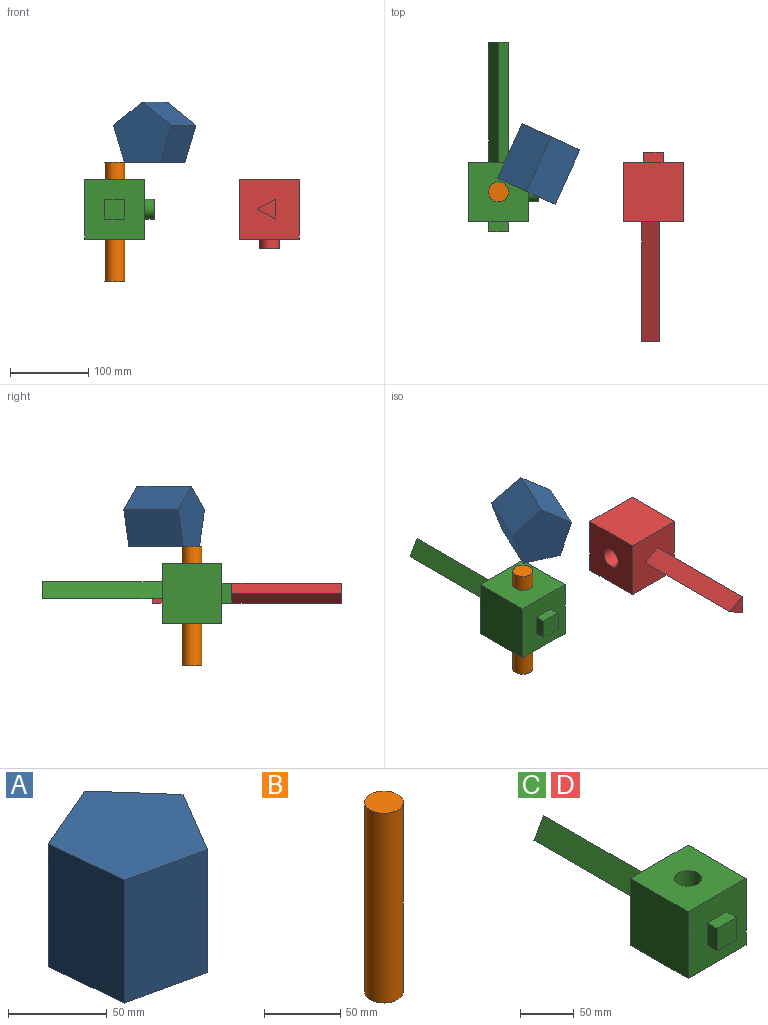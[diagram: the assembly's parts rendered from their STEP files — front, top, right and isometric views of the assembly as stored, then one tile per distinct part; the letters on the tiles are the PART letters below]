
ASSEMBLY  parts=4 mates=3
PART A: 7 faces, bbox 78.8x80.4x76.2 mm
  f0: plane 76.2x37.41mm, normal (0.75,0.66,0), area 3801.5mm2, adj f1,f4,f5,f6
  f1: plane 76.2x45.78mm, normal (-0.4,0.92,0), area 3801.5mm2, adj f0,f2,f5,f6
  f2: plane 76.2x49.66mm, normal (-1,-0.09,0), area 3801.5mm2, adj f1,f3,f5,f6
  f3: plane 76.2x48.69mm, normal (-0.22,-0.98,0), area 3801.5mm2, adj f2,f4,f5,f6
  f4: plane 76.2x42.95mm, normal (0.86,-0.51,0), area 3801.5mm2, adj f0,f3,f5,f6
  f5: plane 80.36x78.79mm, normal (0,0,1), area 4282mm2, adj f0,f1,f2,f3,f4
  f6: plane 80.36x78.79mm, normal (0,0,-1), area 4282mm2, adj f0,f1,f2,f3,f4
PART B: 3 faces, bbox 25.4x25.4x152.4 mm
  f0: cylinder r=12.7mm len=152.4mm, axis (0,0,-1), area 12161mm2, adj f1,f2
  f1: plane 25.4x25.4mm, normal (0,0,1), area 506.7mm2, adj f0
  f2: plane 25.4x25.4mm, normal (0,0,-1), area 506.7mm2, adj f0
PART C: 18 faces, bbox 88.9x241.3x76.2 mm
  f0: plane 76.2x76.2mm, normal (0,-1,0), area 5161.3mm2, adj f1,f2,f3,f4,f7,f8,f9,f10
  f1: plane 76.2x76.2mm, normal (0,0,1), area 5299.7mm2, adj f0,f2,f4,f5,f6
  f2: plane 76.2x76.2mm, normal (-1,0,0), area 5806.4mm2, adj f0,f1,f3,f5
  f3: plane 76.2x76.2mm, normal (0,0,-1), area 5299.7mm2, adj f0,f2,f4,f5,f6
  f4: plane 76.2x76.2mm, normal (1,0,0), area 5299.7mm2, adj f0,f1,f3,f5,f12
  f5: plane 76.2x76.2mm, normal (0,1,0), area 5527.1mm2, adj f1,f2,f3,f4,f14,f15,f16
  f6: cylinder r=12.7mm len=76.2mm, axis (0,0,1), area 6080.5mm2, adj f1,f3
  f7: plane 25.4x12.7mm, normal (0,0,1), area 322.6mm2, adj f0,f8,f10,f11
  f8: plane 25.4x12.7mm, normal (-1,0,0), area 322.6mm2, adj f0,f7,f9,f11
  f9: plane 25.4x12.7mm, normal (0,0,-1), area 322.6mm2, adj f0,f8,f10,f11
  f10: plane 25.4x12.7mm, normal (1,0,0), area 322.6mm2, adj f0,f7,f9,f11
  f11: plane 25.4x25.4mm, normal (0,-1,0), area 645.2mm2, adj f7,f8,f9,f10
  f12: cylinder r=12.7mm len=25.4mm, axis (-1,0,0), area 1013.4mm2, adj f4,f13
  f13: plane 25.4x25.4mm, normal (1,0,0), area 506.7mm2, adj f12
  f14: plane 152.4x25.4mm, normal (0,0,-1), area 3871mm2, adj f5,f15,f16,f17
  f15: plane 152.4x22mm, normal (-0.87,0,0.5), area 3871mm2, adj f5,f14,f16,f17
  f16: plane 152.4x22mm, normal (0.87,0,0.5), area 3871mm2, adj f5,f14,f15,f17
  f17: plane 25.4x22mm, normal (0,1,0), area 279.4mm2, adj f14,f15,f16
PART D: same geometry as C
PLACE A rot(axis=(0.94,-0.32,-0.1),90.6deg) t=(261.73,26.12,175.66)mm
PLACE B t=(-31.11,-5.4,-11.29)mm
PLACE C t=(37.08,66.22,68.2)mm fixed
PLACE D rot(axis=(0.71,0,-0.71),180deg) t=(246.79,-9.98,80.69)mm
MATE slider C.f12 <-> D.f6  axis (1,0,0) through (87.09,28.12,81.48)mm
MATE planar A.f3 <-> B.f0  axis (0,0,-1) through (87.37,63.6,141.11)mm
MATE slider C.f6 <-> B.f0  axis (0,0,1) through (36.29,28.12,119.58)mm
